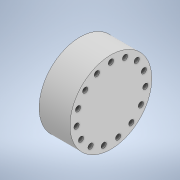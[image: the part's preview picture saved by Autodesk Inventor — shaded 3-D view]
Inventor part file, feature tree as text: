
AUTODESK INVENTOR PART (.ipt)
format: ipt  version: 2021 (Build 250183000, 183)  size: 288,256 bytes
history: native  units: mm
features: extrude x5, sketch x5, other x3, projected_geometry x3
ambient origin geometry x8: Origin, YZ Plane, XZ Plane, XY Plane, X Axis, Y Axis, Z Axis, Center Point
bodies: Solid1 (feature_tree)
feature tree (16):
  other  "wheel_gearing_mount_short.ipt"
  extrude  "Extrusion1"  Depth=10.0mm TaperAngle=0.0deg
  extrude  "Extrusion3"  Depth=5.6mm
  extrude  "Extrusion4"  Depth=6.0mm TaperAngle=0.0deg
  extrude  "Extrusion5"  Depth=10.0mm TaperAngle=0.0deg
  extrude  "Extrusion6"  [1 undecoded]
  other  "Solid1::wheel_gearing_mount_short.ipt"
  other  "TaggingFeature1"
  sketch  "Sketch1"  dims[d0=10.0mm d1=12.0mm d2=0.0mm]
  projected_geometry  "Projected Loop1"
  sketch  "Sketch3"  dims[d7=12.0mm d8=0.0mm d9=5.6mm]
  projected_geometry  "Projected Loop2"
  sketch  "Sketch4"  dims[d10=15.5mm d11=6.0mm d12=0.0mm]
  sketch  "Sketch5"  dims[d13=150.0mm d15=360.0deg d17=10.0mm d18=0.0mm]
  sketch  "Sketch6"  dims[d19=10.0mm d20=0.0mm]
  projected_geometry  "Projected Loop3"
note: 1 required parameter value undecoded (feature->parameter linkage not recoverable at this tier; creation-order binding heuristic only, values carry confidence <= 0.55)
